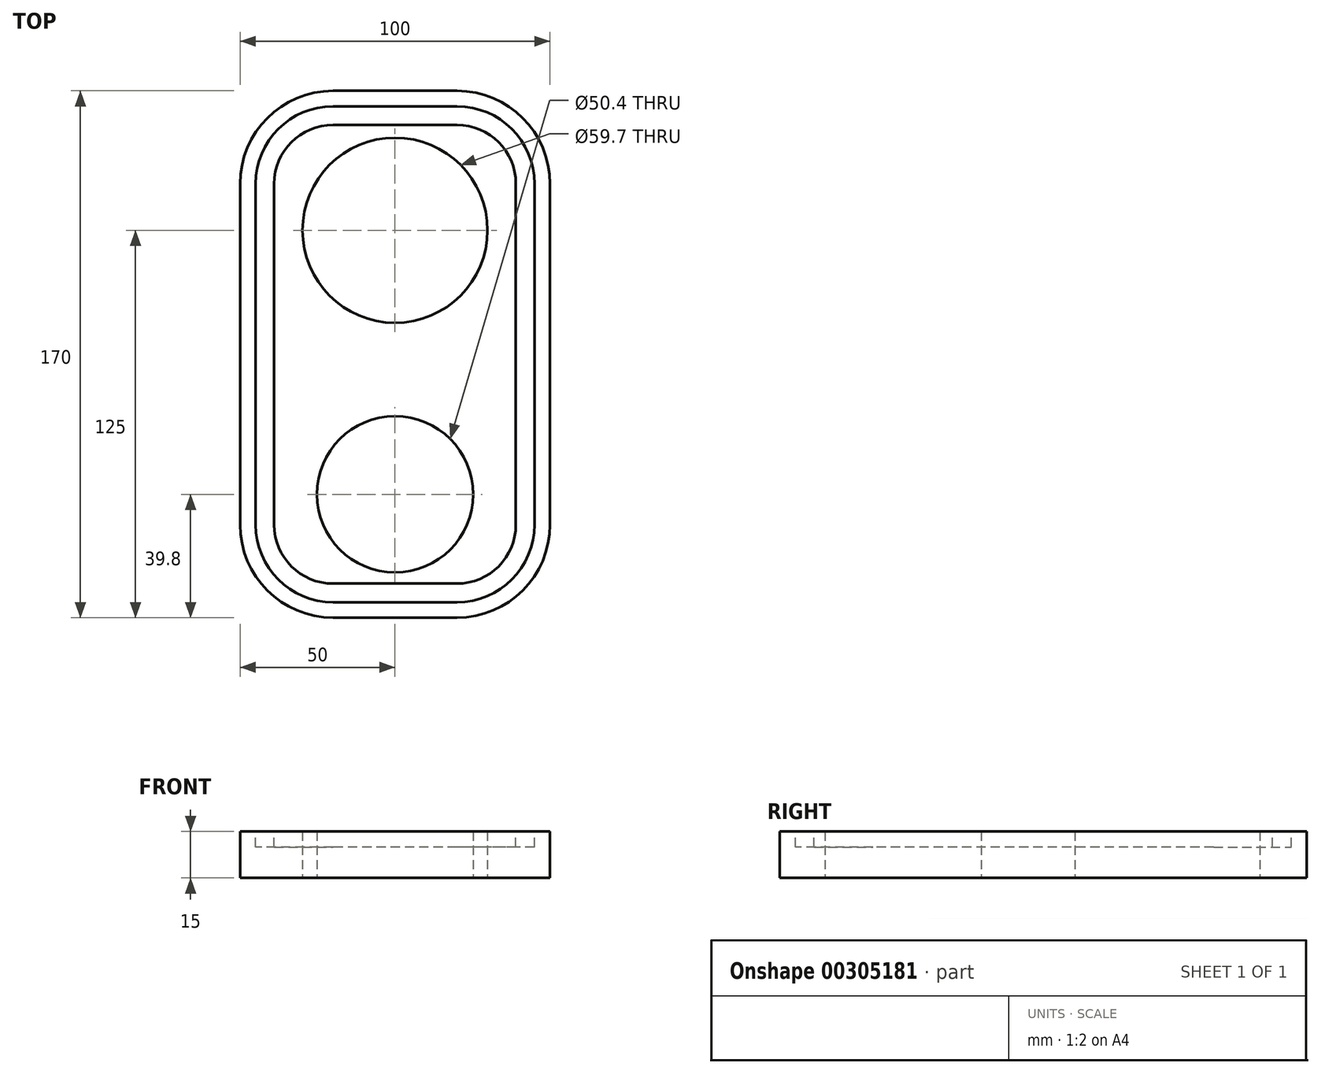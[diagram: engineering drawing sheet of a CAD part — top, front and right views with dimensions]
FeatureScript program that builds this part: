
annotation { "Feature Type Name" : "Feature", "Feature Type Description" : "" }
export const myFeature = defineFeature(function(context is Context, id is Id, definition is map)
    precondition{}
    {
        {
            var Q0;
            Q0=qCreatedBy(makeId("Top.planeOp"),FACE);
            var sketch = newSketch(context, id + "F0", { "sketchPlane" : qUnion([Q0])});
            skLineSegment(sketch, "E0.bottom", {"start": v(50, -85) * mm, "end": v(-50, -85) * mm});
            skLineSegment(sketch, "E0.top", {"start": v(50, 85) * mm, "end": v(-50, 85) * mm});
            skLineSegment(sketch, "E0.left", {"start": v(50, -85) * mm, "end": v(50, 85) * mm});
            skLineSegment(sketch, "E0.right", {"start": v(-50, -85) * mm, "end": v(-50, 85) * mm});
            skPoint(sketch, "E0.middle", {"position": v(0, 0) * mm});
            skLineSegment(sketch, "E1.0", {"start": v(50, 70) * mm, "end": v(-50, 70) * mm});
            skLineSegment(sketch, "E2.0", {"start": v(50, 40) * mm, "end": v(-50, 40) * mm});
            skCircle(sketch, "E3", {"center": v(0, 40) * mm, "radius": 29.85 * mm});
            skCircle(sketch, "E4", {"center": v(0, -45.2) * mm, "radius": 25.2 * mm});
            skSolve(sketch);
        }
        {
            var Q0;
            Q0 = qSketchRegion(id + "F0", true);
            extrude(context, id + "F1", {"entities" : qUnion([Q0]), "depth" : 15 * mm, "offsetDistance" : 25 * mm});
        }
        {
            var Q0;
            Q0=makeQuery(id+"F1.opExtrude","SWEPT_EDGE",EDGE,{"disambiguationData":[OSD([sQuery(id+"F0.wireOp",EDGE,"E0.top"),sQuery(id+"F0.wireOp",EDGE,"E0.right")])]});
            var Q1;
            Q1=makeQuery(id+"F1.opExtrude","SWEPT_EDGE",EDGE,{"disambiguationData":[OSD([sQuery(id+"F0.wireOp",EDGE,"E0.top"),sQuery(id+"F0.wireOp",EDGE,"E0.left")])]});
            var Q2;
            Q2=makeQuery(id+"F1.opExtrude","SWEPT_EDGE",EDGE,{"disambiguationData":[OSD([sQuery(id+"F0.wireOp",EDGE,"E0.bottom"),sQuery(id+"F0.wireOp",EDGE,"E0.right")])]});
            var Q3;
            Q3=makeQuery(id+"F1.opExtrude","SWEPT_EDGE",EDGE,{"disambiguationData":[OSD([sQuery(id+"F0.wireOp",EDGE,"E0.bottom"),sQuery(id+"F0.wireOp",EDGE,"E0.left")])]});
            fillet(context, id + "F2", {"entities" : qUnion([Q0, Q1, Q2, Q3]), "radius" : 30 * mm, "tangentPropagation" : true, "allowEdgeOverflow" : false});
        }
        {
            var Q0;
            Q0=makeQuery(id+"F1.opExtrude","CAP_FACE",FACE,{"disambiguationData":[OSD([sQuery(id+"F0.wireOp",EDGE,"E0.bottom"),sQuery(id+"F0.wireOp",EDGE,"E0.top"),sQuery(id+"F0.wireOp",EDGE,"E0.left"),sQuery(id+"F0.wireOp",EDGE,"E0.right"),sQuery(id+"F0.wireOp",EDGE,"E3"),sQuery(id+"F0.wireOp",EDGE,"E4")])],"isStart":false});
            var sketch = newSketch(context, id + "F3", { "sketchPlane" : qUnion([Q0])});
            skLineSegment(sketch, "E5.0.0", {"start": v(50, -55) * mm, "end": v(50, 55) * mm});
            skArc(sketch, "E5.0.1", {"start": v(50, 55) * mm, "mid": v(41.21, 76.21) * mm, "end": v(20, 85) * mm});
            skLineSegment(sketch, "E5.0.2", {"start": v(20, 85) * mm, "end": v(-20, 85) * mm});
            skArc(sketch, "E5.0.3", {"start": v(-20, 85) * mm, "mid": v(-41.21, 76.21) * mm, "end": v(-50, 55) * mm});
            skLineSegment(sketch, "E5.0.4", {"start": v(-50, 55) * mm, "end": v(-50, -55) * mm});
            skArc(sketch, "E5.0.5", {"start": v(-50, -55) * mm, "mid": v(-41.21, -76.21) * mm, "end": v(-20, -85) * mm});
            skLineSegment(sketch, "E5.0.6", {"start": v(-20, -85) * mm, "end": v(20, -85) * mm});
            skArc(sketch, "E5.0.7", {"start": v(20, -85) * mm, "mid": v(41.21, -76.21) * mm, "end": v(50, -55) * mm});
            skCircle(sketch, "E6.0", {"center": v(0, -45.2) * mm, "radius": 25.2 * mm});
            skCircle(sketch, "E7.0", {"center": v(0, 40) * mm, "radius": 29.85 * mm});
            skSolve(sketch);
        }
        {
            var Q0;
            Q0=makeQuery(id+"F3.imprint","IMPRINT",FACE,{"disambiguationData":[TD([[makeQuery(id+"F3.imprint","IMPRINT",EDGE,{"derivedFrom":sQuery(id+"F3.wireOp",EDGE,"E6.0")}),-1.0]])]});
            var sketch = newSketch(context, id + "F4", { "sketchPlane" : qUnion([Q0])});
            skLineSegment(sketch, "E8.0", {"start": v(20, 80) * mm, "end": v(-20, 80) * mm});
            skArc(sketch, "E8.1", {"start": v(45, 55) * mm, "mid": v(37.68, 72.68) * mm, "end": v(20, 80) * mm});
            skArc(sketch, "E8.2", {"start": v(-20, 80) * mm, "mid": v(-37.68, 72.68) * mm, "end": v(-45, 55) * mm});
            skLineSegment(sketch, "E8.3", {"start": v(45, -55) * mm, "end": v(45, 55) * mm});
            skLineSegment(sketch, "E8.4", {"start": v(-45, 55) * mm, "end": v(-45, -55) * mm});
            skArc(sketch, "E8.5", {"start": v(-45, -55) * mm, "mid": v(-37.68, -72.68) * mm, "end": v(-20, -80) * mm});
            skLineSegment(sketch, "E8.6", {"start": v(-20, -80) * mm, "end": v(20, -80) * mm});
            skArc(sketch, "E8.7", {"start": v(20, -80) * mm, "mid": v(37.68, -72.68) * mm, "end": v(45, -55) * mm});
            skLineSegment(sketch, "E9.0", {"start": v(20, 74) * mm, "end": v(-20, 74) * mm});
            skArc(sketch, "E9.1", {"start": v(39, 55) * mm, "mid": v(33.44, 68.44) * mm, "end": v(20, 74) * mm});
            skArc(sketch, "E9.2", {"start": v(-20, 74) * mm, "mid": v(-33.44, 68.44) * mm, "end": v(-39, 55) * mm});
            skLineSegment(sketch, "E9.3", {"start": v(39, -55) * mm, "end": v(39, 55) * mm});
            skLineSegment(sketch, "E9.4", {"start": v(-39, 55) * mm, "end": v(-39, -55) * mm});
            skArc(sketch, "E9.5", {"start": v(-39, -55) * mm, "mid": v(-33.44, -68.44) * mm, "end": v(-20, -74) * mm});
            skLineSegment(sketch, "E9.6", {"start": v(-20, -74) * mm, "end": v(20, -74) * mm});
            skArc(sketch, "E9.7", {"start": v(20, -74) * mm, "mid": v(33.44, -68.44) * mm, "end": v(39, -55) * mm});
            skSolve(sketch);
        }
        {
            var Q0;
            Q0=makeQuery(id+"F4.imprint","IMPRINT",FACE,{"disambiguationData":[TD([[makeQuery(id+"F4.imprint","IMPRINT",EDGE,{"derivedFrom":sQuery(id+"F4.wireOp",EDGE,"E8.0")}),1.0]])]});
            extrude(context, id + "F5", {"entities" : qUnion([Q0]), "operationType" : NewBodyOperationType.REMOVE, "oppositeDirection" : true, "depth" : 5 * mm, "offsetDistance" : 25 * mm});
        }
    });
